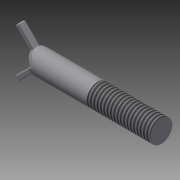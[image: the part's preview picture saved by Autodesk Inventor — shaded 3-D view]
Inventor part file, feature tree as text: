
AUTODESK INVENTOR PART (.ipt)
format: ipt  version: 2014 SP2 (Build 180246200, 246)  size: 254,976 bytes
history: native  units: mm
features: extrude x6, sketch x6, chamfer x2, thread x1, fillet x1
ambient origin geometry x8: Origin, YZ Plane, XZ Plane, XY Plane, X Axis, Y Axis, Z Axis, Center Point
bodies: Solid1 (feature_tree)
feature tree (16):
  extrude  "Extrusion1"  Depth=45.0mm TaperAngle=0.0deg
  thread  "Thread1"  [1 undecoded]
  extrude  "Extrusion2"  Depth=2.0mm
  chamfer  "Chamfer2"  Distance=2.0mm
  extrude  "Extrusion3"  Depth=2.0mm TaperAngle=0.0deg
  extrude  "Extrusion4"  Depth=8.0mm TaperAngle=0.0deg
  extrude  "Extrusion5"  Depth=2.0mm TaperAngle=45.0deg
  extrude  "Extrusion6"  [1 undecoded]
  chamfer  "Chamfer3"  [1 undecoded]
  fillet  "Fillet1"  [1 undecoded]
  sketch  "Sketch1"  dims[d0=8.4mm d1=45.0mm d2=0.0mm d3=24.0mm d4=0.0mm]
  sketch  "Sketch2"  dims[d5=2.0mm d6=2.0mm d7=2.0mm d8=0.0mm]
  sketch  "Sketch3"  dims[d12=2.0mm d13=2.0mm d14=45.0deg d15=2.0mm d16=0.0mm]
  sketch  "Sketch4"  dims[d17=2.0mm d18=0.0mm d19=8.0mm d20=0.0mm]
  sketch  "Sketch5"  dims[d21=8.0mm d22=0.0mm d23=2.0mm d24=2.0mm d25=45.0deg]
  sketch  "Sketch6"  dims[d26=0.5mm]
note: 4 required parameter values undecoded (feature->parameter linkage not recoverable at this tier; creation-order binding heuristic only, values carry confidence <= 0.55)
